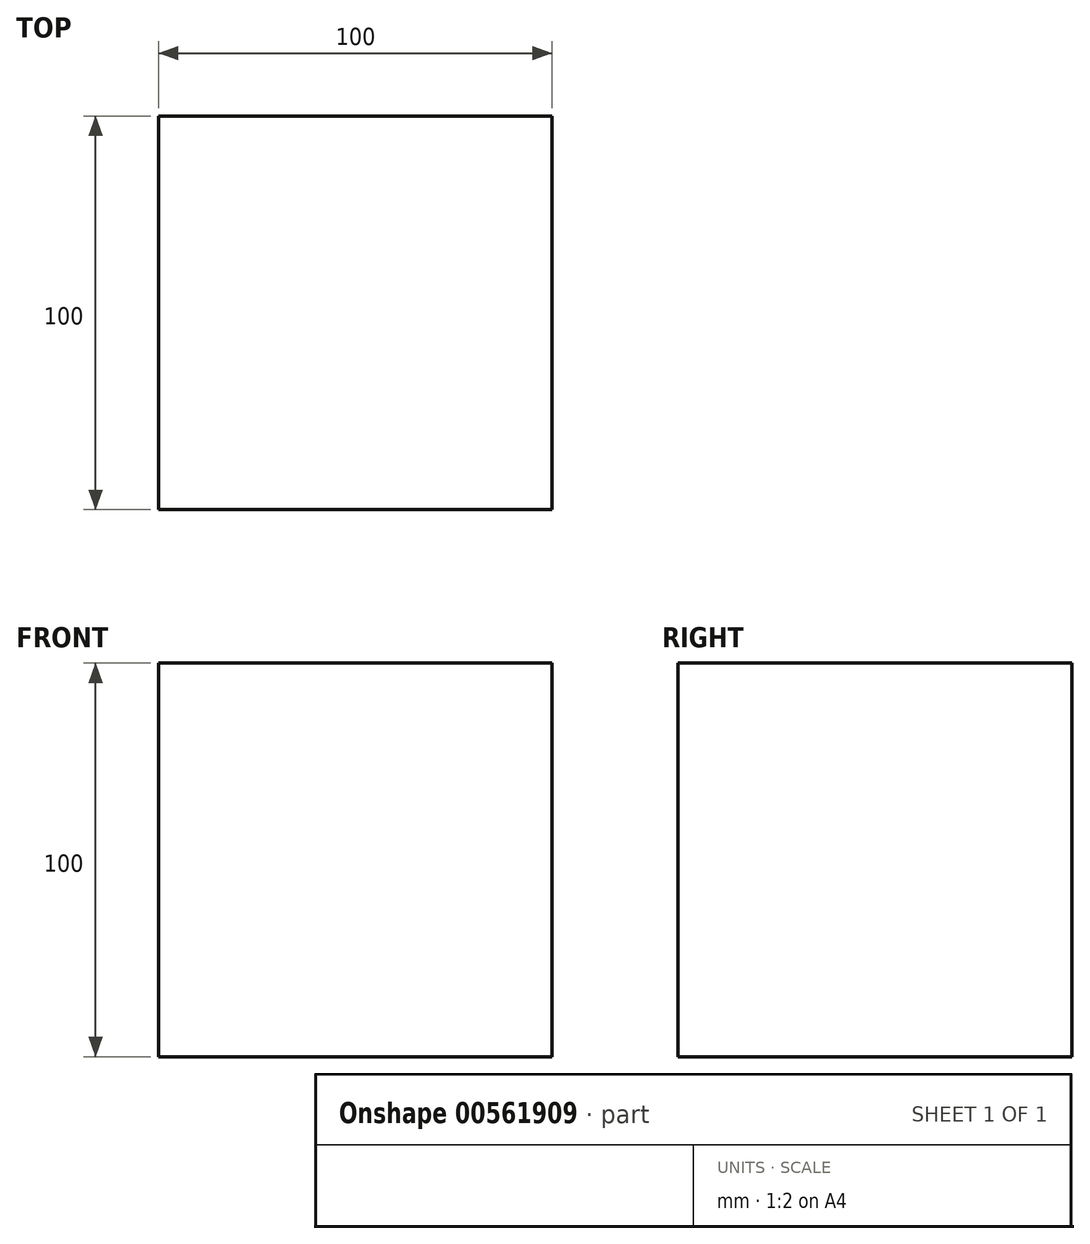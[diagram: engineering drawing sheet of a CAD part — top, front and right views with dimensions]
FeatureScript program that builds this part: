
annotation { "Feature Type Name" : "Feature", "Feature Type Description" : "" }
export const myFeature = defineFeature(function(context is Context, id is Id, definition is map)
    precondition{}
    {
        {
            var Q0;
            Q0=qCreatedBy(makeId("Top.planeOp"),FACE);
            var sketch = newSketch(context, id + "F0", { "sketchPlane" : qUnion([Q0])});
            skLineSegment(sketch, "E0.bottom", {"start": v(0, 0) * mm, "end": v(-100, 0) * mm});
            skLineSegment(sketch, "E0.top", {"start": v(0, 100) * mm, "end": v(-100, 100) * mm});
            skLineSegment(sketch, "E0.left", {"start": v(0, 0) * mm, "end": v(0, 100) * mm});
            skLineSegment(sketch, "E0.right", {"start": v(-100, 0) * mm, "end": v(-100, 100) * mm});
            skSolve(sketch);
        }
        {
            var Q0;
            Q0=makeQuery(id+"F0.imprint","IMPRINT",FACE,{"disambiguationData":[TD([[makeQuery(id+"F0.imprint","IMPRINT",EDGE,{"derivedFrom":sQuery(id+"F0.wireOp",EDGE,"E0.bottom")}),-1.0]])]});
            extrude(context, id + "F1", {"entities" : qUnion([Q0]), "depth" : 100 * mm, "offsetDistance" : 25 * mm});
        }
    });
